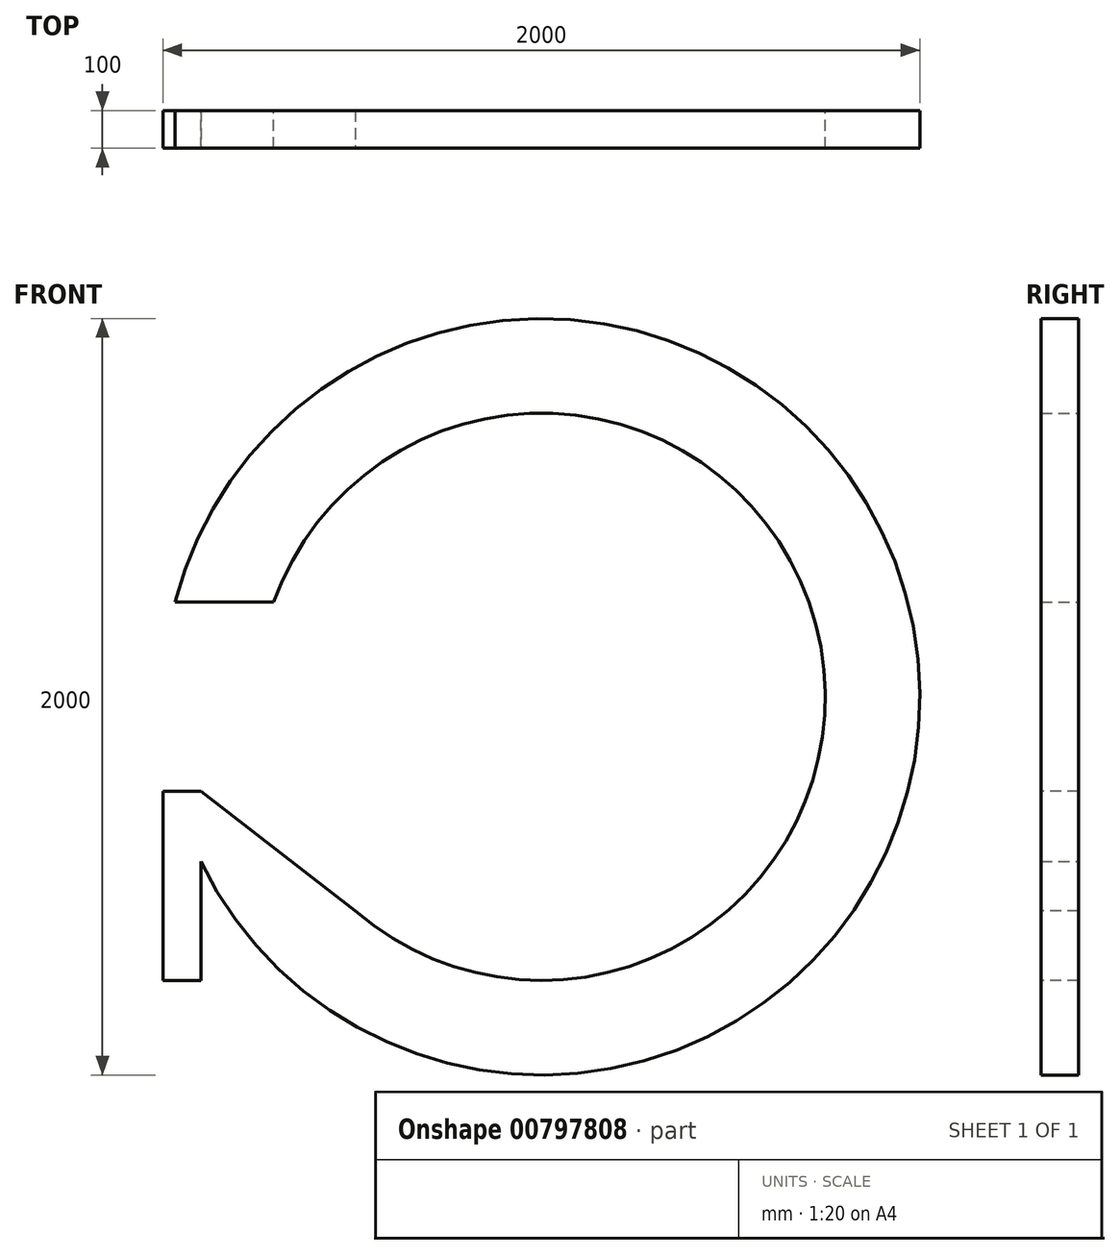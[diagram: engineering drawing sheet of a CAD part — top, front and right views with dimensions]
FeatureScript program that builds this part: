
annotation { "Feature Type Name" : "Feature", "Feature Type Description" : "" }
export const myFeature = defineFeature(function(context is Context, id is Id, definition is map)
    precondition{}
    {
        {
            var Q0;
            Q0=qCreatedBy(makeId("Front.planeOp"),FACE);
            var sketch = newSketch(context, id + "F0", { "sketchPlane" : qUnion([Q0])});
            skCircle(sketch, "E0", {"center": v(0, 0) * mm, "radius": 750 * mm});
            skCircle(sketch, "E1", {"center": v(0, 0) * mm, "radius": 1000 * mm});
            skLineSegment(sketch, "E2", {"start": v(0, 0) * mm, "end": v(0, 1274.48) * mm, "construction": true});
            skLineSegment(sketch, "E3", {"start": v(0, 0) * mm, "end": v(0, -1648.82) * mm, "construction": true});
            skLineSegment(sketch, "E4", {"start": v(0, 0) * mm, "end": v(-1687.62, 0) * mm, "construction": true});
            skLineSegment(sketch, "E5", {"start": v(-968.25, 250) * mm, "end": v(-707.1, 250) * mm});
            skLineSegment(sketch, "E6", {"start": v(-707.1, -250) * mm, "end": v(-968.25, -250) * mm});
            skSolve(sketch);
        }
        {
            var Q0;
            {var subQ0=sQuery(id+"F0.wireOp",EDGE,"E5");Q0=makeQuery(id+"F0.imprint","IMPRINT",FACE,{"disambiguationData":[TD([[makeQuery(id+"F0.imprint","IMPRINT",EDGE,{"derivedFrom":subQ0}),1.0]])]});}
            extrude(context, id + "F1", {"entities" : qUnion([Q0]), "depth" : 100 * mm, "offsetDistance" : 25 * mm});
        }
        {
            var Q0;
            Q0=qCreatedBy(makeId("Right.planeOp"),FACE);
            cPlane(context, id + "F2", {"entities" : qUnion([Q0]), "cplaneType" : CPlaneType.OFFSET, "offset" : 1000 * mm, "oppositeDirection" : true, "width" : 150 * mm, "height" : 150 * mm});
        }
        {
            var Q0;
            Q0=makeQuery(id+"F1.opExtrude","CAP_FACE",FACE,{"disambiguationData":[OSD([sQuery(id+"F0.wireOp",EDGE,"E0"),sQuery(id+"F0.wireOp",EDGE,"E1"),sQuery(id+"F0.wireOp",EDGE,"E5"),sQuery(id+"F0.wireOp",EDGE,"E6")])],"isStart":false});
            var sketch = newSketch(context, id + "F3", { "sketchPlane" : qUnion([Q0])});
            skLineSegment(sketch, "E7", {"start": v(0, 0) * mm, "end": v(1000, 0) * mm, "construction": true});
            skSolve(sketch);
        }
        {
            var Q0;
            Q0=qCreatedBy(id+"F2.planeOp",FACE);
            var sketch = newSketch(context, id + "F4", { "sketchPlane" : qUnion([Q0])});
            skLineSegment(sketch, "E8.bottom", {"start": v(0, -250) * mm, "end": v(-100, -250) * mm});
            skLineSegment(sketch, "E8.top", {"start": v(0, -750) * mm, "end": v(-100, -750) * mm});
            skLineSegment(sketch, "E8.left", {"start": v(0, -250) * mm, "end": v(0, -750) * mm});
            skLineSegment(sketch, "E8.right", {"start": v(-100, -250) * mm, "end": v(-100, -750) * mm});
            skSolve(sketch);
        }
        {
            var Q0;
            Q0=makeQuery(id+"F4.imprint","IMPRINT",FACE,{"disambiguationData":[TD([[makeQuery(id+"F4.imprint","IMPRINT",EDGE,{"derivedFrom":sQuery(id+"F4.wireOp",EDGE,"E8.bottom")}),1.0]])]});
            extrude(context, id + "F5", {"entities" : qUnion([Q0]), "operationType" : NewBodyOperationType.ADD, "depth" : 100 * mm, "offsetDistance" : 25 * mm});
        }
        {
            var Q0;
            Q0=makeQuery(id+"F3.imprint","IMPRINT",FACE,{"disambiguationData":[TD([[makeQuery(id+"F3.imprint","IMPRINT",EDGE,{"derivedFrom":makeQuery(id+"F1.opExtrude","CAP_EDGE",EDGE,{"disambiguationData":[OSD([sQuery(id+"F0.wireOp",EDGE,"E0")])],"isStart":false})}),-1.0]])]});
            var sketch = newSketch(context, id + "F6", { "sketchPlane" : qUnion([Q0])});
            skLineSegment(sketch, "E9", {"start": v(-899.9, -249.66) * mm, "end": v(-470.23, -583.02) * mm});
            skSolve(sketch);
        }
        {
            var Q0;
            {var subQ0=sQuery(id+"F6.wireOp",EDGE,"E9");var subQ1=makeQuery(id+"F3.imprint","IMPRINT",EDGE,{"derivedFrom":makeQuery(id+"F1.opExtrude","CAP_EDGE",EDGE,{"disambiguationData":[OSD([sQuery(id+"F0.wireOp",EDGE,"E0")])],"isStart":false})});var subQ2=makeQuery(id+"F6.imprint","INTERSECT",VERTEX,{"derivedFrom":[subQ1,subQ0]});Q0=makeQuery(id+"F6.imprint","IMPRINT",FACE,{"disambiguationData":[TD([[makeQuery(id+"F6.imprint","IMPRINT",EDGE,{"disambiguationData":[TD([[subQ2,1.0]])],"derivedFrom":subQ0}),1.0]])]});}
            extrude(context, id + "F7", {"entities" : qUnion([Q0]), "operationType" : NewBodyOperationType.REMOVE, "oppositeDirection" : true, "depth" : 100 * mm, "offsetDistance" : 25 * mm});
        }
        {
            var Q0;
            Q0=makeQuery(id+"F5.boolean.opBoolean","MERGE",FACE,{"derivedFrom":[makeQuery(id+"F1.opExtrude","SWEPT_FACE",FACE,{"disambiguationData":[OSD([sQuery(id+"F0.wireOp",EDGE,"E6")])]}),makeQuery(id+"F5.opExtrude","SWEPT_FACE",FACE,{"disambiguationData":[OSD([sQuery(id+"F4.wireOp",EDGE,"E8.bottom")])]})]});
            var sketch = newSketch(context, id + "F8", { "sketchPlane" : qUnion([Q0])});
            skLineSegment(sketch, "E10", {"start": v(-899.47, 0) * mm, "end": v(-1000, -100) * mm, "construction": true});
            skLineSegment(sketch, "E11", {"start": v(-1000, -100) * mm, "end": v(-899.47, -100) * mm, "construction": true});
            skLineSegment(sketch, "E12", {"start": v(-899.47, -100) * mm, "end": v(-1000, 0) * mm, "construction": true});
            skLineSegment(sketch, "E13", {"start": v(-1000, 0) * mm, "end": v(-899.47, 0) * mm, "construction": true});
            skLineSegment(sketch, "E14", {"start": v(-899.47, -100) * mm, "end": v(-1000, -100) * mm, "construction": true});
            skSolve(sketch);
        }
    });
